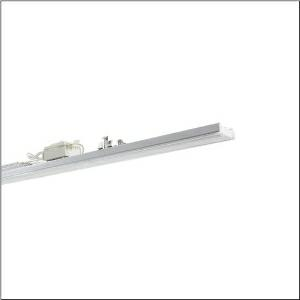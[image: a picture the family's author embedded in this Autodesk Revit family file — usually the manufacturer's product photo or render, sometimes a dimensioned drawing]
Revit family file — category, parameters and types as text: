
# Revit family: licross_11_recessed_mo_51te19mn495g
name_source: partatom
category: Lighting Fixtures
units: mm (PartAtom-declared; Revit-internal decimal feet)

## family parameters
Cut with Voids When Loaded = No
Host = Face
Light Source = No
Part Type = Normal
Room Calculation Point = No
Round Connector Dimension = Use Diameter
Shared = No

## types (1)
- --- (1 x LED, 9850 lm, 55.2 W, 4000K)
    Apparent Load = 55 VA
    CIE Flux Codes = 55 90 98 100 100
    Color Rendering = 80
    Color Temperature = 4000K
    Default Elevation = 1800 mm
    Description = Licross 11 Recessed MO, luminaire insert, of sheet steel, galvanised, coil coated, white, length: 1.500mm, width: 66mm, height: 67mm, LED rated luminous flux: 9.860lm, light colour: 840, SDCM (Standard Deviation of Colour Matching)MacAdam ≤ 2 SDCM (initial), control gear: ON/OFF Multilumen, with plug, 3-pole, with phase selection, mains connection: 220..240V, AC, 50/60Hz, rated input power: 55W, internal wiring halogen-free, primary light control with lens, of plastic, primary optical cover: cover, of PMMA, light emission: direct distribution, primary light characteristic: double asymmetric, protection rating (complete): IP54, insulation class (complete): insulation class I (protective earthing), certification: CE, ENEC, VDE, UKCA, protection symbol: D if used in an environment with non-conductive dust loads with corresponding accessories, impact resistance: IK06, permissible ambient temperature for indoor applications: -35..+40°C, corresponds to IFS (International Featured Standards) requirements for safety and quality in the food industry, reducing of maximum allowable ambient temperature of 5°C with ceiling mounting, The light source and the operating device comply with the requirements of the Ecodesign Regulation (EU) 2019/2020 and are replaceable in accordance with this regulation, packaging unit: 1 piece
    Height = 58 mm
    Lamp = 1 x LED
    Lamp Light Flux = 9850 lm
    Lamp Power = 55.2 W
    Lamp count = 1
    Length = 1500 mm
    Luminous efficacy = 178 lm/W
    Manufacturer = Siteco
    ModVariant = No
    Model = 51TE19MN495G
    Mounting Place = Ceiling
    Mounting Type = Pendant
    Number of Poles = 1
    OnlyDefault = Yes
    Power Factor = 1
    Product Name = Licross 11 Recessed MO
    Product group = luminaire insert | ceiling pendant
    ProductGroupID = 901
    Protection Class = Protection class I
    Protection Degree = IP 54
    RLX_Detail_Level = 1
    RLX_Emergency_Light_Flux = 0 lm
    RLX_Emergency_Type = 0
    RLX_Emergency_Type_DB = No
    RlxData = <blob elided: 22493 chars, md5=70a2f958>
    Socket = socket
    Standby Power = 0 W
    System Light Flux = 9850 lm
    System Power = 55 W
    Type Comments = factory setting: luminous flux: 100 % | (A | C | E) | 126 mA
    Type Image = l_1296930.jpg
    URL = http://relux.com
    VarID = @adj_090319
    Voltage = 0 V
    Weight = 0.00 kg
    Width = 66 mm

## geometry (parser evidence)
native form markers: Blend x4, Sweep x11
no freeform markers — native parametric forms only
